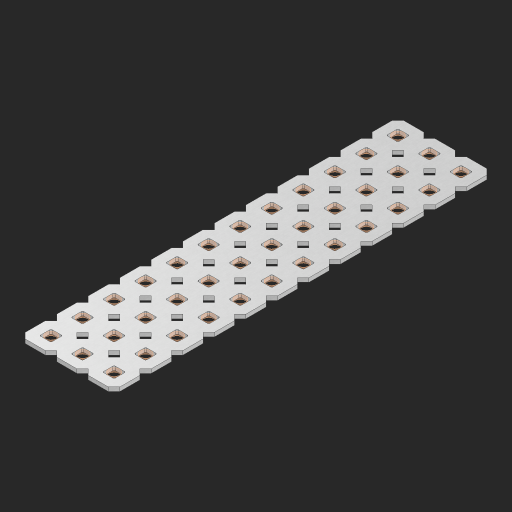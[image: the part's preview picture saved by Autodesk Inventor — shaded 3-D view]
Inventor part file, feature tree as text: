
AUTODESK INVENTOR PART (.ipt)
format: ipt  version: 2023 (Build 270158000, 158)  size: 701,952 bytes
history: native  units: in
note: dims shown in document units (in); Inventor stores cm internally (conversion verified against a paired STEP export)
features: other x37, extrude x35, sketch x2, pattern_linear x1
ambient origin geometry x8: Origin, YZ Plane, XZ Plane, XY Plane, X Axis, Y Axis, Z Axis, Center Point
bodies: Solid1 (feature_tree), Body (feature_tree)
feature tree (75):
  pattern_linear  "Rectangular Pattern1"  Spacing1=0.09in  [1 undecoded]
  sketch  "Sketch1"  dims[d1=0.5in]
  sketch  "Sketch2"  dims[d2=0.182in d3=0.09in d4=0.09in d5=0.09in d6=0.09in d7=0.09in d8=0.09in d9=0.09in d10=0.09in d11=0.02in d13=0.0in d14=0.172in d15=0.0625in d16=0.0in d19=0.5in d22=0.5in]
  other  "Srf1"
  other  "Srf126"
  other  "Srf127"
  other  "Srf128"
  other  "Srf129"
  other  "Srf130"
  other  "Srf131"
  other  "Srf250"
  other  "Srf251"
  other  "Srf252"
  other  "Srf253"
  other  "Srf254"
  other  "Srf268"
  other  "Srf269"
  other  "Srf270"
  other  "Srf271"
  other  "Srf272"
  other  "Srf273"
  other  "Srf274"
  other  "Srf275"
  other  "Srf276"
  other  "Srf277"
  other  "Srf278"
  other  "Srf279"
  other  "Srf293"
  other  "Srf294"
  other  "Srf295"
  other  "Srf296"
  other  "Srf297"
  other  "Srf298"
  other  "Srf299"
  other  "Srf300"
  other  "Srf301"
  other  "Srf302"
  other  "Srf303"
  other  "Srf304"
  other  "Circle"
  extrude  "ExtrusionSrf126"  Depth=0.09in
  extrude  "ExtrusionSrf127"  Depth=0.09in
  extrude  "ExtrusionSrf128"  Depth=0.09in
  extrude  "ExtrusionSrf129"  Depth=0.09in
  extrude  "ExtrusionSrf130"  Depth=0.09in
  extrude  "ExtrusionSrf131"  Depth=0.09in
  extrude  "ExtrusionSrf250"  Depth=0.09in
  extrude  "ExtrusionSrf251"  Depth=0.02in
  extrude  "ExtrusionSrf252"  TaperAngle=0.0deg  [1 undecoded]
  extrude  "ExtrusionSrf253"  Depth=0.5in
  extrude  "ExtrusionSrf254"  Depth=0.0625in TaperAngle=0.0deg
  extrude  "ExtrusionSrf268"  Depth=0.5in
  extrude  "ExtrusionSrf269"  Depth=0.5in
  extrude  "ExtrusionSrf270"  [1 undecoded]
  extrude  "ExtrusionSrf271"  [1 undecoded]
  extrude  "ExtrusionSrf272"  [1 undecoded]
  extrude  "ExtrusionSrf273"  [1 undecoded]
  extrude  "ExtrusionSrf274"  [1 undecoded]
  extrude  "ExtrusionSrf275"  [1 undecoded]
  extrude  "ExtrusionSrf276"  [1 undecoded]
  extrude  "ExtrusionSrf277"  [1 undecoded]
  extrude  "ExtrusionSrf278"  [1 undecoded]
  extrude  "ExtrusionSrf279"  [1 undecoded]
  extrude  "ExtrusionSrf293"  [1 undecoded]
  extrude  "ExtrusionSrf294"  [1 undecoded]
  extrude  "ExtrusionSrf295"  [1 undecoded]
  extrude  "ExtrusionSrf296"  [1 undecoded]
  extrude  "ExtrusionSrf297"  [1 undecoded]
  extrude  "ExtrusionSrf298"  [1 undecoded]
  extrude  "ExtrusionSrf299"  [1 undecoded]
  extrude  "ExtrusionSrf300"  [1 undecoded]
  extrude  "ExtrusionSrf301"  [1 undecoded]
  extrude  "ExtrusionSrf302"  [1 undecoded]
  extrude  "ExtrusionSrf303"  [1 undecoded]
  extrude  "ExtrusionSrf304"  [1 undecoded]
note: 24 required parameter values undecoded (feature->parameter linkage not recoverable at this tier; creation-order binding heuristic only, values carry confidence <= 0.55)
